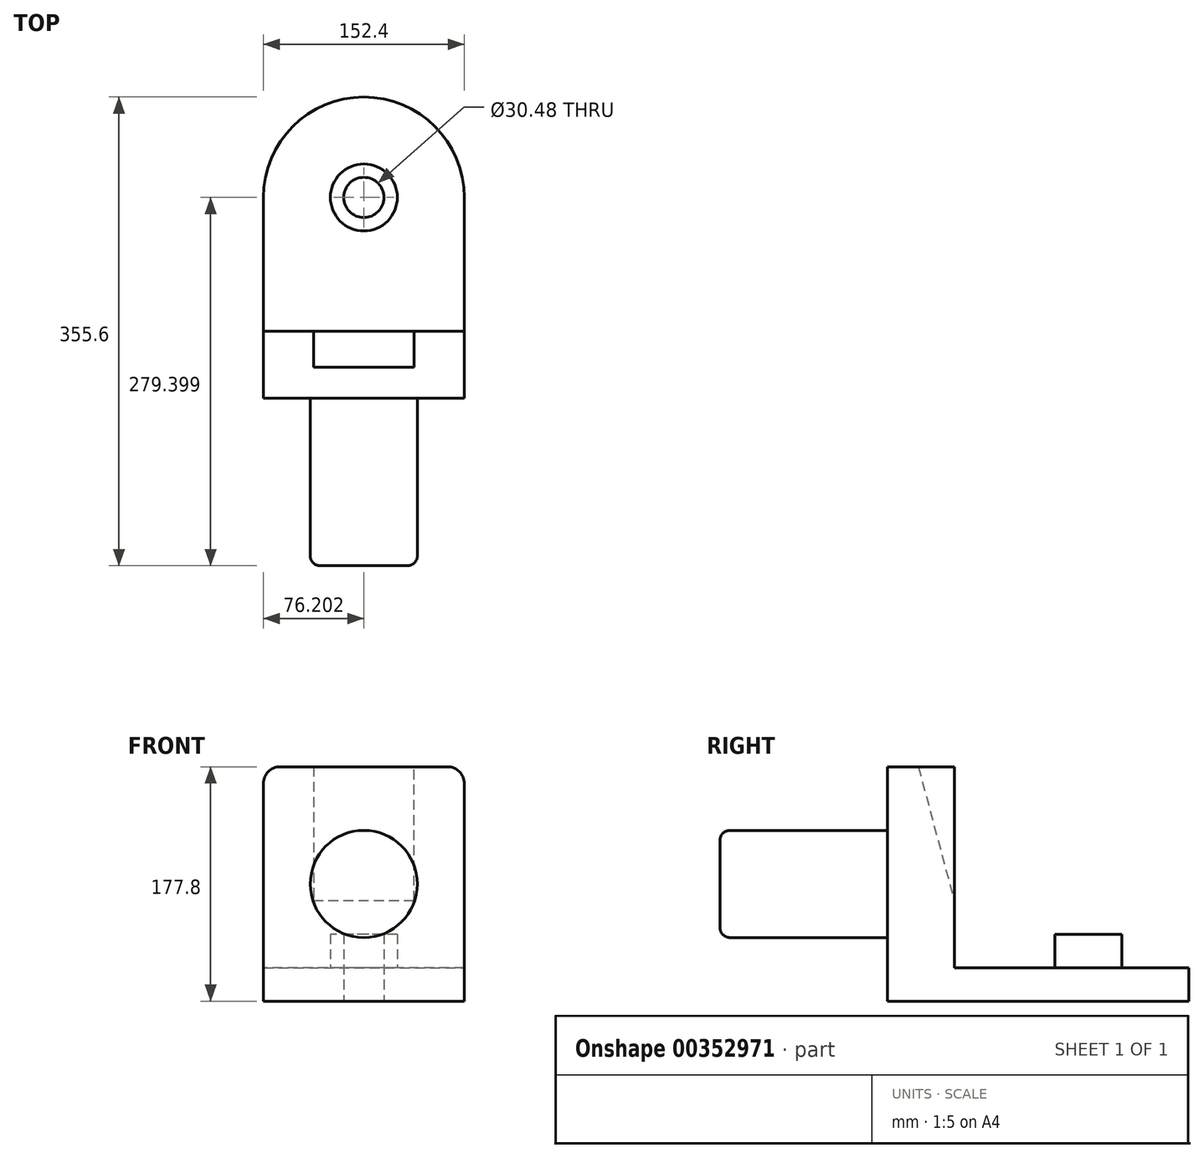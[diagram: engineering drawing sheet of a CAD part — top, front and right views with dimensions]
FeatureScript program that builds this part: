
annotation { "Feature Type Name" : "Feature", "Feature Type Description" : "" }
export const myFeature = defineFeature(function(context is Context, id is Id, definition is map)
    precondition{}
    {
        {
            var Q0;
            Q0=qCreatedBy(makeId("Top.planeOp"),FACE);
            var sketch = newSketch(context, id + "F0", { "sketchPlane" : qUnion([Q0])});
            skLineSegment(sketch, "E0", {"start": v(38.18, 130.68) * mm, "end": v(38.18, 130.68) * mm});
            skLineSegment(sketch, "E1", {"start": v(114.38, 54.48) * mm, "end": v(114.38, -47.12) * mm});
            skLineSegment(sketch, "E2", {"start": v(114.38, -47.12) * mm, "end": v(114.38, -97.92) * mm});
            skLineSegment(sketch, "E3", {"start": v(114.38, -97.92) * mm, "end": v(-38.02, -97.92) * mm});
            skLineSegment(sketch, "E4", {"start": v(-38.02, -97.92) * mm, "end": v(-38.02, -47.12) * mm});
            skLineSegment(sketch, "E5", {"start": v(-38.02, -47.12) * mm, "end": v(114.38, -47.12) * mm});
            skLineSegment(sketch, "E6", {"start": v(-38.02, -47.12) * mm, "end": v(-38.02, 54.48) * mm});
            skPoint(sketch, "E7.visualSharp", {"position": v(114.38, 130.68) * mm});
            skArc(sketch, "E7.filletArc", {"start": v(114.38, 54.48) * mm, "mid": v(92.06, 108.36) * mm, "end": v(38.18, 130.68) * mm});
            skPoint(sketch, "E8.visualSharp", {"position": v(-38.02, 130.68) * mm});
            skArc(sketch, "E8.filletArc", {"start": v(38.18, 130.68) * mm, "mid": v(-15.7, 108.36) * mm, "end": v(-38.02, 54.48) * mm});
            skCircle(sketch, "E9", {"center": v(38.18, 54.48) * mm, "radius": 15.24 * mm});
            skCircle(sketch, "E10", {"center": v(38.18, 54.48) * mm, "radius": 25.4 * mm});
            skSolve(sketch);
        }
        {
            var Q0;
            Q0=makeQuery(id+"F0.imprint","IMPRINT",FACE,{"disambiguationData":[TD([[makeQuery(id+"F0.imprint","IMPRINT",EDGE,{"derivedFrom":sQuery(id+"F0.wireOp",EDGE,"E9")}),-1.0]])]});
            extrude(context, id + "F1", {"entities" : qUnion([Q0]), "depth" : 50.8 * mm});
        }
        {
            var Q0;
            Q0=makeQuery(id+"F0.imprint","IMPRINT",FACE,{"disambiguationData":[TD([[makeQuery(id+"F0.imprint","IMPRINT",EDGE,{"derivedFrom":sQuery(id+"F0.wireOp",EDGE,"E1")}),-1.0]])]});
            extrude(context, id + "F2", {"entities" : qUnion([Q0]), "operationType" : NewBodyOperationType.ADD, "depth" : 25.4 * mm});
        }
        {
            var Q0;
            Q0=makeQuery(id+"F0.imprint","IMPRINT",FACE,{"disambiguationData":[TD([[makeQuery(id+"F0.imprint","IMPRINT",EDGE,{"derivedFrom":sQuery(id+"F0.wireOp",EDGE,"E2")}),-1.0]])]});
            extrude(context, id + "F3", {"entities" : qUnion([Q0]), "operationType" : NewBodyOperationType.ADD, "depth" : 177.8 * mm});
        }
        {
            var Q0;
            Q0=makeQuery(id+"F3.opExtrude","SWEPT_FACE",FACE,{"disambiguationData":[OSD([sQuery(id+"F0.wireOp",EDGE,"E3")])]});
            var sketch = newSketch(context, id + "F4", { "sketchPlane" : qUnion([Q0])});
            skLineSegment(sketch, "E11", {"start": v(-38.02, 88.9) * mm, "end": v(-38.02, 177.8) * mm});
            skPoint(sketch, "E12.endSnap0", {"position": v(38.18, 0) * mm});
            skCircle(sketch, "E13", {"center": v(38.18, 88.9) * mm, "radius": 40.64 * mm});
            skPoint(sketch, "E14.end.orphan", {"position": v(-38.02, 88.9) * mm});
            skSolve(sketch);
        }
        {
            var Q0;
            Q0=makeQuery(id+"F4.imprint","IMPRINT",FACE,{"disambiguationData":[TD([[makeQuery(id+"F4.imprint","IMPRINT",EDGE,{"derivedFrom":sQuery(id+"F4.wireOp",EDGE,"E13")}),1.0]])]});
            extrude(context, id + "F5", {"entities" : qUnion([Q0]), "operationType" : NewBodyOperationType.ADD, "depth" : 127 * mm});
        }
        {
            var Q0;
            Q0=makeQuery(id+"F5.opExtrude","CAP_EDGE",EDGE,{"disambiguationData":[OSD([sQuery(id+"F4.wireOp",EDGE,"E13")])],"isStart":false});
            fillet(context, id + "F6", {"entities" : qUnion([Q0]), "radius" : 7.62 * mm, "tangentPropagation" : true, "allowEdgeOverflow" : false});
        }
        {
            var Q0;
            Q0=makeQuery(id+"F3.boolean.opBoolean","MERGE",FACE,{"derivedFrom":[makeQuery(id+"F2.opExtrude","SWEPT_FACE",FACE,{"disambiguationData":[OSD([sQuery(id+"F0.wireOp",EDGE,"E1")])]}),makeQuery(id+"F3.opExtrude","SWEPT_FACE",FACE,{"disambiguationData":[OSD([sQuery(id+"F0.wireOp",EDGE,"E2")])]})]});
            var sketch = newSketch(context, id + "F7", { "sketchPlane" : qUnion([Q0])});
            skLineSegment(sketch, "E15", {"start": v(-47.12, 177.8) * mm, "end": v(-47.12, 76.2) * mm});
            skLineSegment(sketch, "E16", {"start": v(-47.12, 76.2) * mm, "end": v(-74.34, 177.8) * mm});
            skLineSegment(sketch, "E17", {"start": v(-74.34, 177.8) * mm, "end": v(-47.12, 177.8) * mm});
            skSolve(sketch);
        }
        {
            var Q0;
            Q0=makeQuery(id+"F3.boolean.opBoolean","MERGE",FACE,{"derivedFrom":[makeQuery(id+"F2.opExtrude","SWEPT_FACE",FACE,{"disambiguationData":[OSD([sQuery(id+"F0.wireOp",EDGE,"E6")])]}),makeQuery(id+"F3.opExtrude","SWEPT_FACE",FACE,{"disambiguationData":[OSD([sQuery(id+"F0.wireOp",EDGE,"E4")])]})]});
            var sketch = newSketch(context, id + "F8", { "sketchPlane" : qUnion([Q0])});
            skLineSegment(sketch, "E18", {"start": v(47.12, 177.8) * mm, "end": v(47.12, 76.2) * mm});
            skPoint(sketch, "E19.end.orphan", {"position": v(72.52, 177.8) * mm});
            skLineSegment(sketch, "E20", {"start": v(47.12, 76.2) * mm, "end": v(74.34, 177.8) * mm});
            skSolve(sketch);
        }
        {
            var Q0;
            {var subQ0=sQuery(id+"F8.wireOp",EDGE,"E18");Q0=makeQuery(id+"F8.imprint","IMPRINT",FACE,{"disambiguationData":[TD([[makeQuery(id+"F8.imprint","IMPRINT",EDGE,{"derivedFrom":subQ0}),1.0]])]});}
            extrude(context, id + "F9", {"entities" : qUnion([Q0]), "operationType" : NewBodyOperationType.REMOVE, "oppositeDirection" : true, "depth" : 164.85 * mm});
        }
        {
            var Q0;
            {var subQ4=sQuery(id+"F7.wireOp",EDGE,"E16");Q0=makeQuery(id+"F7.imprint","IMPRINT",FACE,{"disambiguationData":[TD([[makeQuery(id+"F7.imprint","IMPRINT",EDGE,{"derivedFrom":subQ4}),1.0]])]});}
            var Q1;
            Q1=makeQuery(id+"F7.imprint","IMPRINT",FACE,{"disambiguationData":[TD([[makeQuery(id+"F7.imprint","IMPRINT",EDGE,{"derivedFrom":sQuery(id+"F7.wireOp",EDGE,"E15")}),-1.0]])]});
            extrude(context, id + "F10", {"entities" : qUnion([Q0, Q1]), "operationType" : NewBodyOperationType.ADD, "oppositeDirection" : true, "depth" : 38.1 * mm});
        }
        {
            var Q0;
            {var subQ0=sQuery(id+"F8.wireOp",EDGE,"E18");Q0=makeQuery(id+"F8.imprint","IMPRINT",FACE,{"disambiguationData":[TD([[makeQuery(id+"F8.imprint","IMPRINT",EDGE,{"derivedFrom":subQ0}),1.0]])]});}
            var Q1;
            {var subQ4=sQuery(id+"F8.wireOp",EDGE,"E20");Q1=makeQuery(id+"F8.imprint","IMPRINT",FACE,{"disambiguationData":[TD([[makeQuery(id+"F8.imprint","IMPRINT",EDGE,{"derivedFrom":subQ4}),-1.0]])]});}
            extrude(context, id + "F11", {"entities" : qUnion([Q0, Q1]), "operationType" : NewBodyOperationType.ADD, "oppositeDirection" : true, "depth" : 38.1 * mm});
        }
        {
            var Q0;
            {var subQ0=sQuery(id+"F0.wireOp",EDGE,"E2");Q0=makeQuery(id+"F10.boolean.opBoolean","MERGE",EDGE,{"derivedFrom":[makeQuery(id+"F3.opExtrude","CAP_EDGE",EDGE,{"disambiguationData":[OSD([subQ0])],"isStart":false}),makeQuery(id+"F10.opExtrude","CAP_EDGE",EDGE,{"disambiguationData":[OSD([subQ0,sQuery(id+"F7.wireOp",EDGE,"E17")])],"isStart":true})]});}
            var Q1;
            {var subQ0=sQuery(id+"F0.wireOp",EDGE,"E4");Q1=makeQuery(id+"F11.boolean.opBoolean","MERGE",EDGE,{"derivedFrom":[makeQuery(id+"F3.opExtrude","CAP_EDGE",EDGE,{"disambiguationData":[OSD([subQ0])],"isStart":false}),makeQuery(id+"F11.opExtrude","CAP_EDGE",EDGE,{"disambiguationData":[OSD([subQ0])],"isStart":true})]});}
            fillet(context, id + "F12", {"entities" : qUnion([Q0, Q1]), "radius" : 12.7 * mm, "tangentPropagation" : true, "allowEdgeOverflow" : false});
        }
    });
